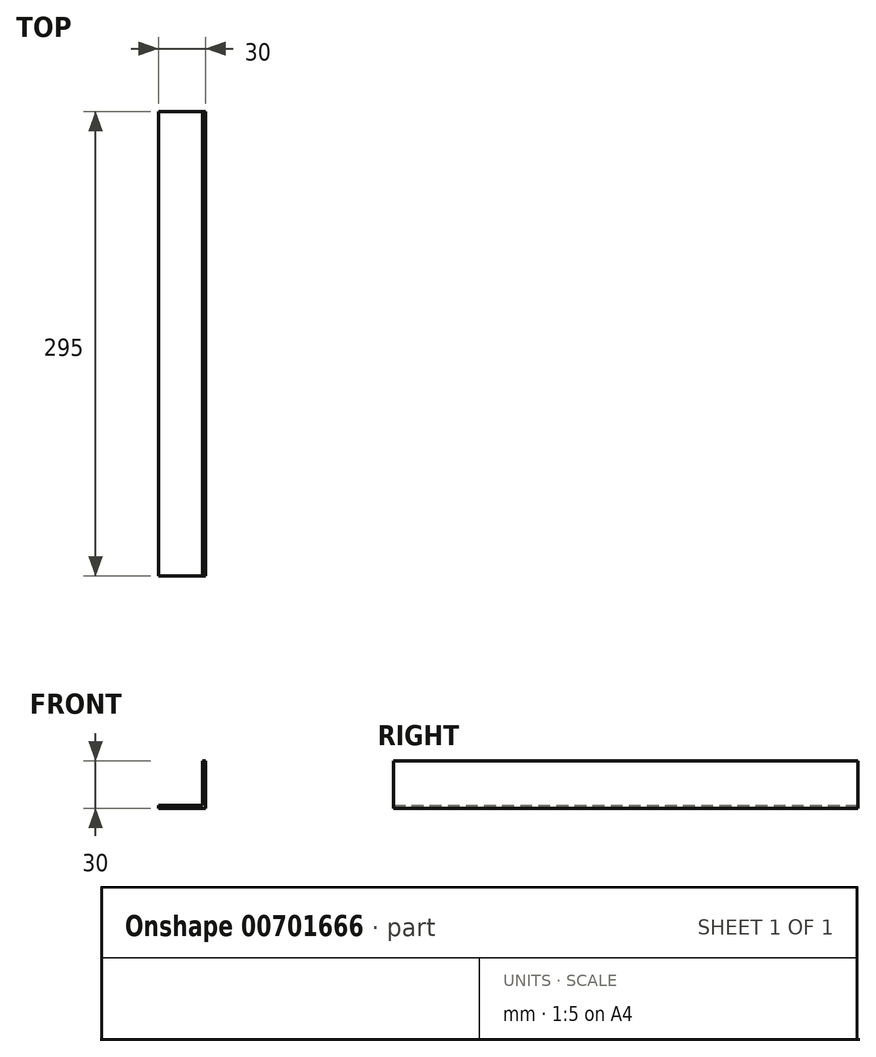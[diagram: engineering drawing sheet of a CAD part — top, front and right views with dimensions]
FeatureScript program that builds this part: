
annotation { "Feature Type Name" : "Feature", "Feature Type Description" : "" }
export const myFeature = defineFeature(function(context is Context, id is Id, definition is map)
    precondition{}
    {
        {
            var Q0;
            Q0=qCreatedBy(makeId("Front.planeOp"),FACE);
            var sketch = newSketch(context, id + "F0", { "sketchPlane" : qUnion([Q0])});
            skLineSegment(sketch, "E0", {"start": v(0, 0) * mm, "end": v(0, 30) * mm});
            skLineSegment(sketch, "E1", {"start": v(0, 0) * mm, "end": v(-30, 0) * mm});
            skLineSegment(sketch, "E2", {"start": v(-30, 0) * mm, "end": v(-30, 2) * mm});
            skLineSegment(sketch, "E3", {"start": v(-30, 2) * mm, "end": v(-2, 2) * mm});
            skLineSegment(sketch, "E4", {"start": v(-2, 2) * mm, "end": v(-2, 30) * mm});
            skLineSegment(sketch, "E5", {"start": v(-2, 30) * mm, "end": v(0, 30) * mm});
            skSolve(sketch);
        }
        {
            var Q0;
            Q0=makeQuery(id+"F0.imprint","IMPRINT",FACE,{"disambiguationData":[TD([[makeQuery(id+"F0.imprint","IMPRINT",EDGE,{"derivedFrom":sQuery(id+"F0.wireOp",EDGE,"E0")}),1.0]])]});
            extrude(context, id + "F1", {"entities" : qUnion([Q0]), "endBound" : BoundingType.SYMMETRIC, "depth" : 295 * mm, "offsetDistance" : 25 * mm});
        }
    });
